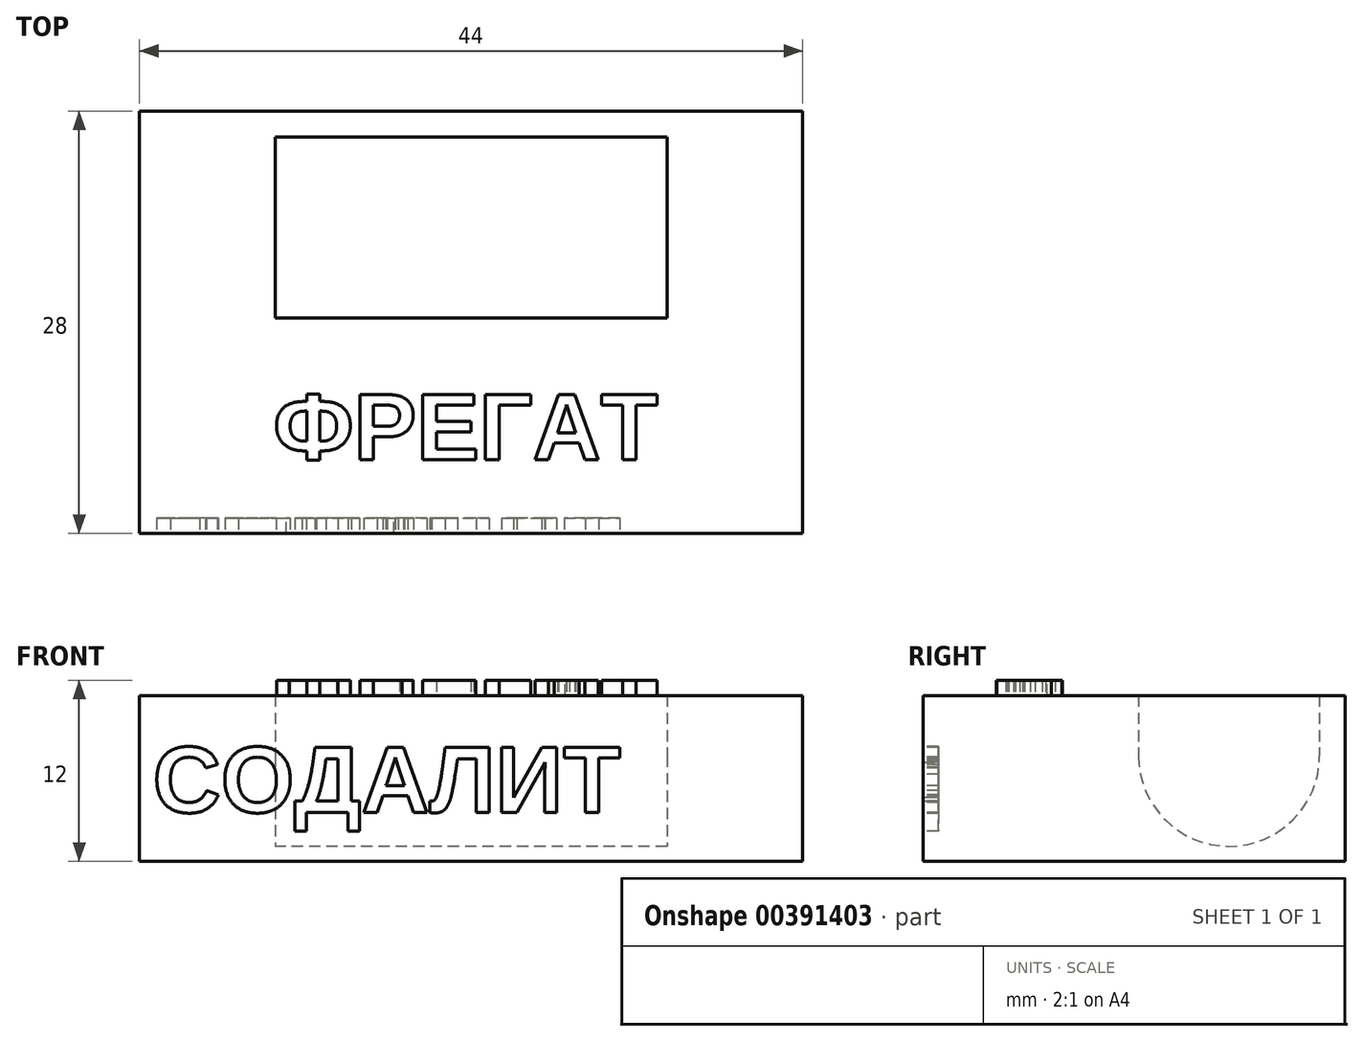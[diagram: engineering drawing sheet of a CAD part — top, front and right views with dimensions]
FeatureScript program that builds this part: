
annotation { "Feature Type Name" : "Feature", "Feature Type Description" : "" }
export const myFeature = defineFeature(function(context is Context, id is Id, definition is map)
    precondition{}
    {
        {
            assignVariable(context, id + "F0", {"name" : "len", "anyValue" : 21});
        }
        {
            assignVariable(context, id + "F1", {"name" : "dia", "anyValue" : 10});
        }
        {
            var Q0;
            Q0=qCreatedBy(makeId("Top.planeOp"),FACE);
            var sketch = newSketch(context, id + "F2", { "sketchPlane" : qUnion([Q0])});
            skLineSegment(sketch, "E0.bottom", {"start": v(0, 0) * mm, "end": v(44, 0) * mm});
            skLineSegment(sketch, "E0.top", {"start": v(0, 28) * mm, "end": v(44, 28) * mm});
            skLineSegment(sketch, "E0.left", {"start": v(0, 0) * mm, "end": v(0, 28) * mm});
            skLineSegment(sketch, "E0.right", {"start": v(44, 0) * mm, "end": v(44, 28) * mm});
            skSolve(sketch);
        }
        {
            var Q0;
            Q0 = qSketchRegion(id + "F2", true);
            extrude(context, id + "F3", {"entities" : qUnion([Q0]), "offsetDistance" : 25 * mm, "depth" : (getVariable(context, 'dia') + 1) * mm});
        }
        {
            var Q0;
            Q0=makeQuery(id+"F3.opExtrude","SWEPT_FACE",FACE,{"disambiguationData":[OSD([sQuery(id+"F2.wireOp",EDGE,"E0.left")])]});
            var Q1;
            Q1=makeQuery(id+"F3.opExtrude","SWEPT_FACE",FACE,{"disambiguationData":[OSD([sQuery(id+"F2.wireOp",EDGE,"E0.right")])]});
            cPlane(context, id + "F4", {"entities" : qUnion([Q0, Q1]), "cplaneType" : CPlaneType.MID_PLANE, "offset" : 25 * mm, "width" : 150 * mm, "height" : 150 * mm});
        }
        {
            var Q0;
            Q0=qCreatedBy(id+"F4.planeOp",FACE);
            var sketch = newSketch(context, id + "F5", { "sketchPlane" : qUnion([Q0])});
            skLineSegment(sketch, "E1", {"start": v(-26.3, 11) * mm, "end": v(-26.3, 7) * mm});
            skLineSegment(sketch, "E2", {"start": v(-14.3, 11) * mm, "end": v(-14.3, 7) * mm});
            skLineSegment(sketch, "E3.0.0", {"start": v(-28, 0) * mm, "end": v(0, 0) * mm});
            skLineSegment(sketch, "E3.0.1", {"start": v(0, 0) * mm, "end": v(0, 11) * mm});
            skLineSegment(sketch, "E3.0.2", {"start": v(0, 11) * mm, "end": v(-28, 11) * mm});
            skLineSegment(sketch, "E3.0.3", {"start": v(-28, 11) * mm, "end": v(-28, 0) * mm});
            skArc(sketch, "E4", {"start": v(-26.3, 7) * mm, "mid": v(-20.3, 1) * mm, "end": v(-14.3, 7) * mm});
            skPoint(sketch, "E5", {"position": v(-20.3, 1) * mm});
            skSolve(sketch);
        }
        {
            var Q0;
            {var subQ0=sQuery(id+"F5.wireOp",EDGE,"E1");Q0=makeQuery(id+"F5.imprint","IMPRINT",FACE,{"disambiguationData":[TD([[makeQuery(id+"F5.imprint","IMPRINT",EDGE,{"derivedFrom":subQ0}),1.0]])]});}
            var Q1;
            Q1=qCreatedBy(id+"FSk3R6doaHebItA_1.planeOp",FACE);
            extrude(context, id + "F6", {"entities" : qUnion([Q0]), "operationType" : NewBodyOperationType.REMOVE, "endBound" : BoundingType.SYMMETRIC, "oppositeDirection" : true, "endBoundEntityFace" : qUnion([Q1]), "offsetDistance" : 25 * mm, "depth" : (getVariable(context, 'len') + 5) * mm});
        }
        {
            var Q0;
            Q0=makeQuery(id+"F3.opExtrude","CAP_FACE",FACE,{"disambiguationData":[OSD([sQuery(id+"F2.wireOp",EDGE,"E0.bottom"),sQuery(id+"F2.wireOp",EDGE,"E0.top"),sQuery(id+"F2.wireOp",EDGE,"E0.left"),sQuery(id+"F2.wireOp",EDGE,"E0.right")])],"isStart":false});
            var sketch = newSketch(context, id + "F7", { "sketchPlane" : qUnion([Q0])});
            skText(sketch, "E6", { "text": "ОБИТЕЛЬ", "fontName": "Arimo-Bold.ttf"});
            skText(sketch, "E7", { "text": "ЗЛА", "fontName": "Arimo-Bold.ttf"});
            skLineSegment(sketch, "E8", {"start": v(22, 14.3) * mm, "end": v(22, 0) * mm, "construction": true});
            const initialGuessF7  = {"E6": [0.00654, 0.0082, 1, 0, 0.0045], "E7": [0.009, 0.002, 1, 0, 0.0045]};
            skSetInitialGuess(sketch, initialGuessF7);
            skSolve(sketch);
        }
        {
            var Q0;
            Q0=makeQuery(id+"F3.opExtrude","SWEPT_FACE",FACE,{"disambiguationData":[OSD([sQuery(id+"F2.wireOp",EDGE,"E0.bottom")])]});
            var sketch = newSketch(context, id + "F8", { "sketchPlane" : qUnion([Q0])});
            skText(sketch, "E9", { "text": "СОДАЛИТ", "fontName": "Arimo-Bold.ttf"});
            skLineSegment(sketch, "E10", {"start": v(22, 11) * mm, "end": v(22, 0) * mm, "construction": true});
            skPoint(sketch, "E11", {"position": v(22, 5.5) * mm});
            const initialGuessF8  = {"E9": [0.00089, 0.00325, 1, 0, 0.0045]};
            skSetInitialGuess(sketch, initialGuessF8);
            skSolve(sketch);
        }
        {
            var Q0;
            Q0 = qSketchRegion(id + "F8", true);
            extrude(context, id + "F9", {"entities" : qUnion([Q0]), "operationType" : NewBodyOperationType.REMOVE, "oppositeDirection" : true, "depth" : 1 * mm});
        }
        {
            var Q0;
            {var subQ30=sQuery(id+"F2.wireOp",EDGE,"E0.bottom");var subQ53=sQuery(id+"F2.wireOp",EDGE,"E0.top");var subQ60=sQuery(id+"F2.wireOp",EDGE,"E0.right");var subQ61=sQuery(id+"F2.wireOp",EDGE,"E0.left");Q0=makeQuery(id+"FYv7Y7HDNhZfK1O_1.boolean.opBoolean","SPLIT",FACE,{"disambiguationData":[TD([makeQuery(id+"F3.opExtrude","SWEPT_FACE",FACE,{"disambiguationData":[OSD([subQ30])]})])],"derivedFrom":makeQuery(id+"F3.opExtrude","CAP_FACE",FACE,{"disambiguationData":[OSD([subQ30,subQ53,subQ61,subQ60])],"isStart":false})});}
            var sketch = newSketch(context, id + "F10", { "sketchPlane" : qUnion([Q0])});
            skLineSegment(sketch, "E12", {"start": v(22, 14.3) * mm, "end": v(22, 0) * mm, "construction": true});
            skText(sketch, "E13", { "text": "ФРЕГАТ", "fontName": "Arimo-Bold.ttf"});
            skPoint(sketch, "E14", {"position": v(22, 7.15) * mm});
            const initialGuessF10  = {"E13": [0.00887, 0.0049, 1, 0, 0.0045]};
            skSetInitialGuess(sketch, initialGuessF10);
            skSolve(sketch);
        }
        {
            var Q0;
            Q0 = qSketchRegion(id + "F10", true);
            extrude(context, id + "F11", {"entities" : qUnion([Q0]), "operationType" : NewBodyOperationType.ADD, "depth" : 1 * mm});
        }
    });
